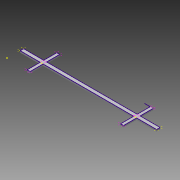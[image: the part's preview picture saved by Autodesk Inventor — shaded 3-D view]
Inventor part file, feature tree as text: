
AUTODESK INVENTOR PART (.ipt)
format: ipt  version: 2015 (Build 190159000, 159)  size: 119,808 bytes
history: native  units: mm
features: extrude x4, sketch x4, plane x3
ambient origin geometry x8: Origin, YZ Plane, XZ Plane, XY Plane, X Axis, Y Axis, Z Axis, Center Point
bodies: Solid1 (feature_tree)
feature tree (11):
  plane  "Work Plane4"
  extrude  "Extrusion2"  Depth=3.0mm TaperAngle=0.0deg
  plane  "Work Plane8"
  sketch  "Sketch3"  dims[d7=5.0mm d13=5.0mm]
  plane  "Work Plane9"
  sketch  "Sketch5"  dims[d14=3.0mm d15=0.0mm d16=3.0mm d17=0.0mm]
  extrude  "Extrusion5"  Depth=5.0mm
  extrude  "Extrusion6"  Depth=3.0mm TaperAngle=0.0deg
  extrude  "Extrusion7"  [1 undecoded]
  sketch  "Sketch7"  dims[d18=3.0mm d19=0.0mm]
  sketch  "Sketch2"  dims[d4=6.0mm d5=3.0mm d6=0.0mm]
note: 1 required parameter value undecoded (feature->parameter linkage not recoverable at this tier; creation-order binding heuristic only, values carry confidence <= 0.55)
